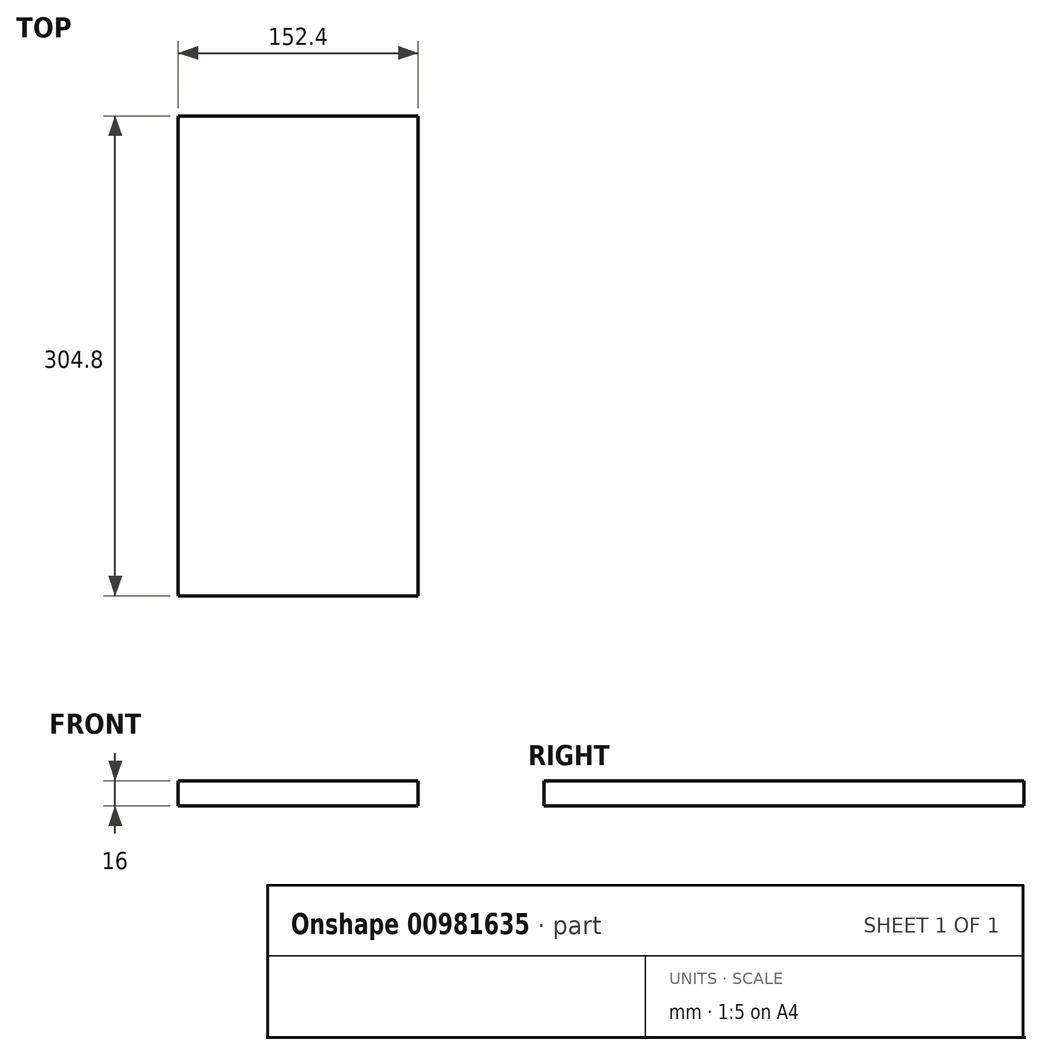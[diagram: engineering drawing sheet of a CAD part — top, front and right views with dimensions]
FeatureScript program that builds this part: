
annotation { "Feature Type Name" : "Feature", "Feature Type Description" : "" }
export const myFeature = defineFeature(function(context is Context, id is Id, definition is map)
    precondition{}
    {
        {
            var Q0;
            Q0=qCreatedBy(makeId("Top.planeOp"),FACE);
            var sketch = newSketch(context, id + "F0", { "sketchPlane" : qUnion([Q0])});
            skLineSegment(sketch, "E0.bottom", {"start": v(-64.17, 243.68) * mm, "end": v(88.23, 243.68) * mm});
            skLineSegment(sketch, "E0.top", {"start": v(-64.17, -61.12) * mm, "end": v(88.23, -61.12) * mm});
            skLineSegment(sketch, "E0.left", {"start": v(-64.17, 243.68) * mm, "end": v(-64.17, -61.12) * mm});
            skLineSegment(sketch, "E0.right", {"start": v(88.23, 243.68) * mm, "end": v(88.23, -61.12) * mm});
            skSolve(sketch);
        }
        {
            var Q0;
            Q0 = qSketchRegion(id + "F0", true);
            extrude(context, id + "F1", {"entities" : qUnion([Q0]), "depth" : 16 * mm, "offsetDistance" : 25 * mm});
        }
    });
